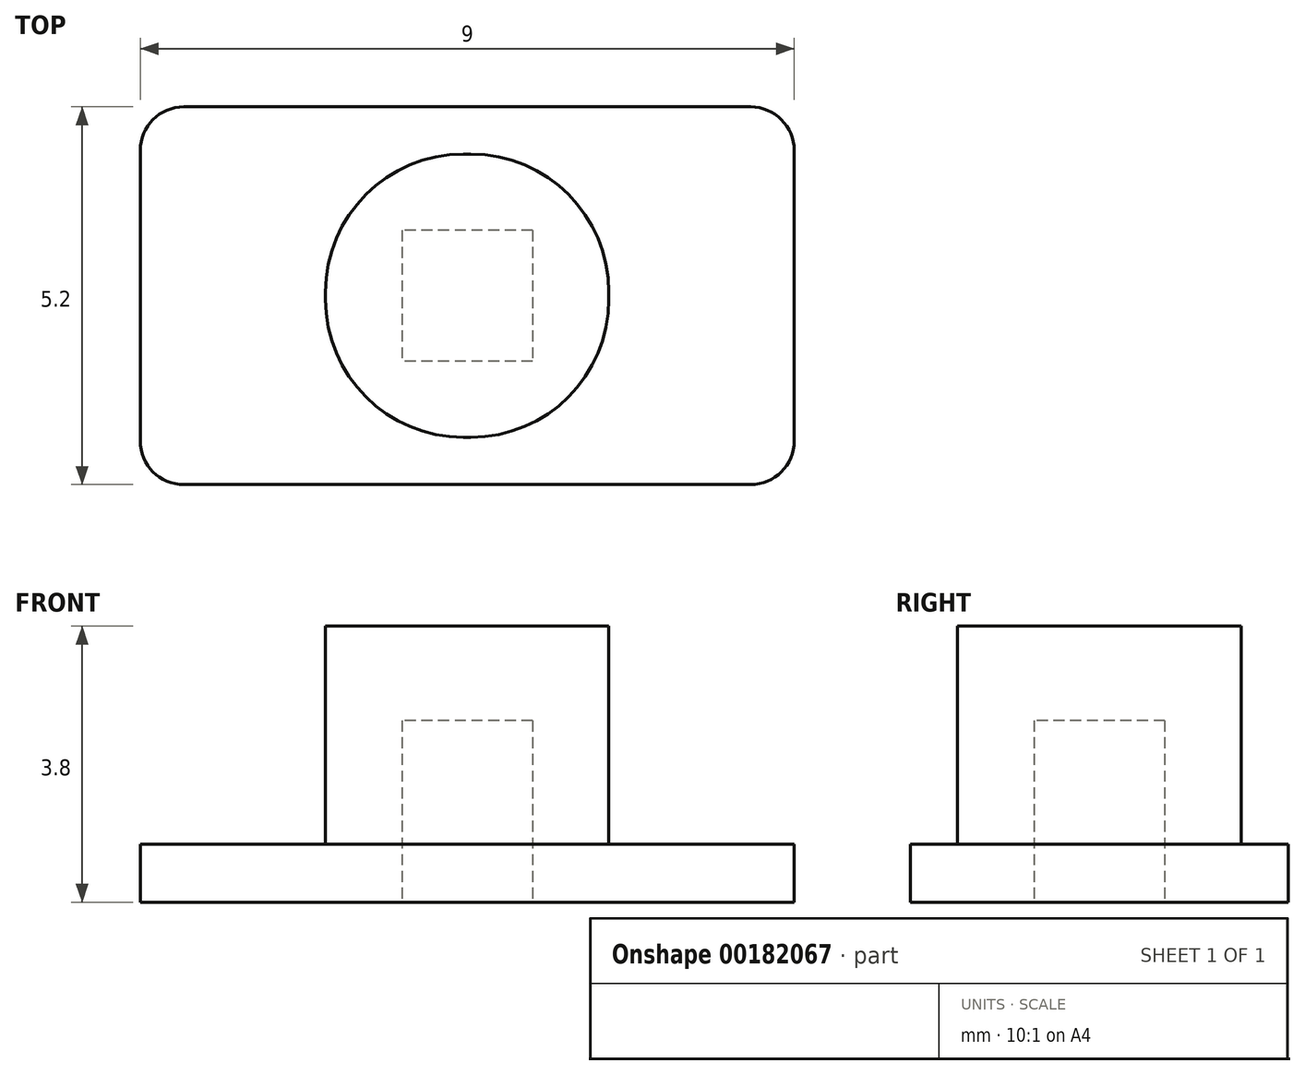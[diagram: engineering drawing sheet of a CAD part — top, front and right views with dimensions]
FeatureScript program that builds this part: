
annotation { "Feature Type Name" : "Feature", "Feature Type Description" : "" }
export const myFeature = defineFeature(function(context is Context, id is Id, definition is map)
    precondition{}
    {
        {
            var Q0;
            Q0=qCreatedBy(makeId("Top.planeOp"),FACE);
            var sketch = newSketch(context, id + "F0", { "sketchPlane" : qUnion([Q0])});
            skLineSegment(sketch, "E0.bottom", {"start": v(4.5, -2.6) * mm, "end": v(-4.5, -2.6) * mm});
            skLineSegment(sketch, "E0.top", {"start": v(4.5, 2.6) * mm, "end": v(-4.5, 2.6) * mm});
            skLineSegment(sketch, "E0.left", {"start": v(4.5, -2.6) * mm, "end": v(4.5, 2.6) * mm});
            skLineSegment(sketch, "E0.right", {"start": v(-4.5, -2.6) * mm, "end": v(-4.5, 2.6) * mm});
            skPoint(sketch, "E0.middle", {"position": v(0, 0) * mm});
            skSolve(sketch);
        }
        {
            var Q0;
            Q0=qSketchRegion(id+"F0",true);
            extrude(context, id + "F1", {"entities" : qUnion([Q0]), "depth" : 0.8 * mm});
        }
        {
            var Q0;
            Q0=makeQuery(id+"F1.opExtrude","CAP_FACE",FACE,{"disambiguationData":[OSD([sQuery(id+"F0.wireOp",EDGE,"E0.bottom"),sQuery(id+"F0.wireOp",EDGE,"E0.top"),sQuery(id+"F0.wireOp",EDGE,"E0.left"),sQuery(id+"F0.wireOp",EDGE,"E0.right")])],"isStart":false});
            var sketch = newSketch(context, id + "F2", { "sketchPlane" : qUnion([Q0])});
            skLineSegment(sketch, "E1.bottom", {"start": v(-1.95, 1.95) * mm, "end": v(1.95, 1.95) * mm});
            skLineSegment(sketch, "E1.top", {"start": v(-1.95, -1.95) * mm, "end": v(1.95, -1.95) * mm});
            skLineSegment(sketch, "E1.left", {"start": v(-1.95, 1.95) * mm, "end": v(-1.95, -1.95) * mm});
            skLineSegment(sketch, "E1.right", {"start": v(1.95, 1.95) * mm, "end": v(1.95, -1.95) * mm});
            skPoint(sketch, "E1.middle", {"position": v(0, 0) * mm});
            skSolve(sketch);
        }
        {
            var Q0;
            Q0=qSketchRegion(id+"F2",true);
            extrude(context, id + "F3", {"entities" : qUnion([Q0]), "operationType" : NewBodyOperationType.ADD, "depth" : 3 * mm});
        }
        {
            var Q0;
            Q0=makeQuery(id+"F3.opExtrude","SWEPT_EDGE",EDGE,{"disambiguationData":[OSD([sQuery(id+"F2.wireOp",EDGE,"E1.top"),sQuery(id+"F2.wireOp",EDGE,"E1.left")])]});
            var Q1;
            Q1=makeQuery(id+"F3.opExtrude","SWEPT_EDGE",EDGE,{"disambiguationData":[OSD([sQuery(id+"F2.wireOp",EDGE,"E1.bottom"),sQuery(id+"F2.wireOp",EDGE,"E1.left")])]});
            var Q2;
            Q2=makeQuery(id+"F3.opExtrude","SWEPT_EDGE",EDGE,{"disambiguationData":[OSD([sQuery(id+"F2.wireOp",EDGE,"E1.top"),sQuery(id+"F2.wireOp",EDGE,"E1.right")])]});
            var Q3;
            Q3=makeQuery(id+"F3.opExtrude","SWEPT_EDGE",EDGE,{"disambiguationData":[OSD([sQuery(id+"F2.wireOp",EDGE,"E1.bottom"),sQuery(id+"F2.wireOp",EDGE,"E1.right")])]});
            fillet(context, id + "F4", {"entities" : qUnion([Q0, Q1, Q2, Q3]), "radius" : 1.9 * mm, "tangentPropagation" : true, "allowEdgeOverflow" : false});
        }
        {
            var Q0;
            Q0=makeQuery(id+"F1.opExtrude","SWEPT_EDGE",EDGE,{"disambiguationData":[OSD([sQuery(id+"F0.wireOp",EDGE,"E0.bottom"),sQuery(id+"F0.wireOp",EDGE,"E0.right")])]});
            var Q1;
            Q1=makeQuery(id+"F1.opExtrude","SWEPT_EDGE",EDGE,{"disambiguationData":[OSD([sQuery(id+"F0.wireOp",EDGE,"E0.top"),sQuery(id+"F0.wireOp",EDGE,"E0.right")])]});
            var Q2;
            Q2=makeQuery(id+"F1.opExtrude","SWEPT_EDGE",EDGE,{"disambiguationData":[OSD([sQuery(id+"F0.wireOp",EDGE,"E0.bottom"),sQuery(id+"F0.wireOp",EDGE,"E0.left")])]});
            var Q3;
            Q3=makeQuery(id+"F1.opExtrude","SWEPT_EDGE",EDGE,{"disambiguationData":[OSD([sQuery(id+"F0.wireOp",EDGE,"E0.top"),sQuery(id+"F0.wireOp",EDGE,"E0.left")])]});
            fillet(context, id + "F5", {"entities" : qUnion([Q0, Q1, Q2, Q3]), "radius" : 0.6 * mm, "tangentPropagation" : true, "allowEdgeOverflow" : false});
        }
        {
            var Q0;
            Q0=makeQuery(id+"F1.opExtrude","CAP_FACE",FACE,{"disambiguationData":[OSD([sQuery(id+"F0.wireOp",EDGE,"E0.bottom"),sQuery(id+"F0.wireOp",EDGE,"E0.top"),sQuery(id+"F0.wireOp",EDGE,"E0.left"),sQuery(id+"F0.wireOp",EDGE,"E0.right")])],"isStart":true});
            var sketch = newSketch(context, id + "F6", { "sketchPlane" : qUnion([Q0])});
            skLineSegment(sketch, "E2.bottom", {"start": v(0.9, -0.9) * mm, "end": v(-0.9, -0.9) * mm});
            skLineSegment(sketch, "E2.top", {"start": v(0.9, 0.9) * mm, "end": v(-0.9, 0.9) * mm});
            skLineSegment(sketch, "E2.left", {"start": v(0.9, -0.9) * mm, "end": v(0.9, 0.9) * mm});
            skLineSegment(sketch, "E2.right", {"start": v(-0.9, -0.9) * mm, "end": v(-0.9, 0.9) * mm});
            skPoint(sketch, "E2.middle", {"position": v(0, 0) * mm});
            skSolve(sketch);
        }
        {
            var Q0;
            Q0=qSketchRegion(id+"F6",true);
            extrude(context, id + "F7", {"entities" : qUnion([Q0]), "operationType" : NewBodyOperationType.REMOVE, "oppositeDirection" : true, "depth" : 2.5 * mm});
        }
    });
